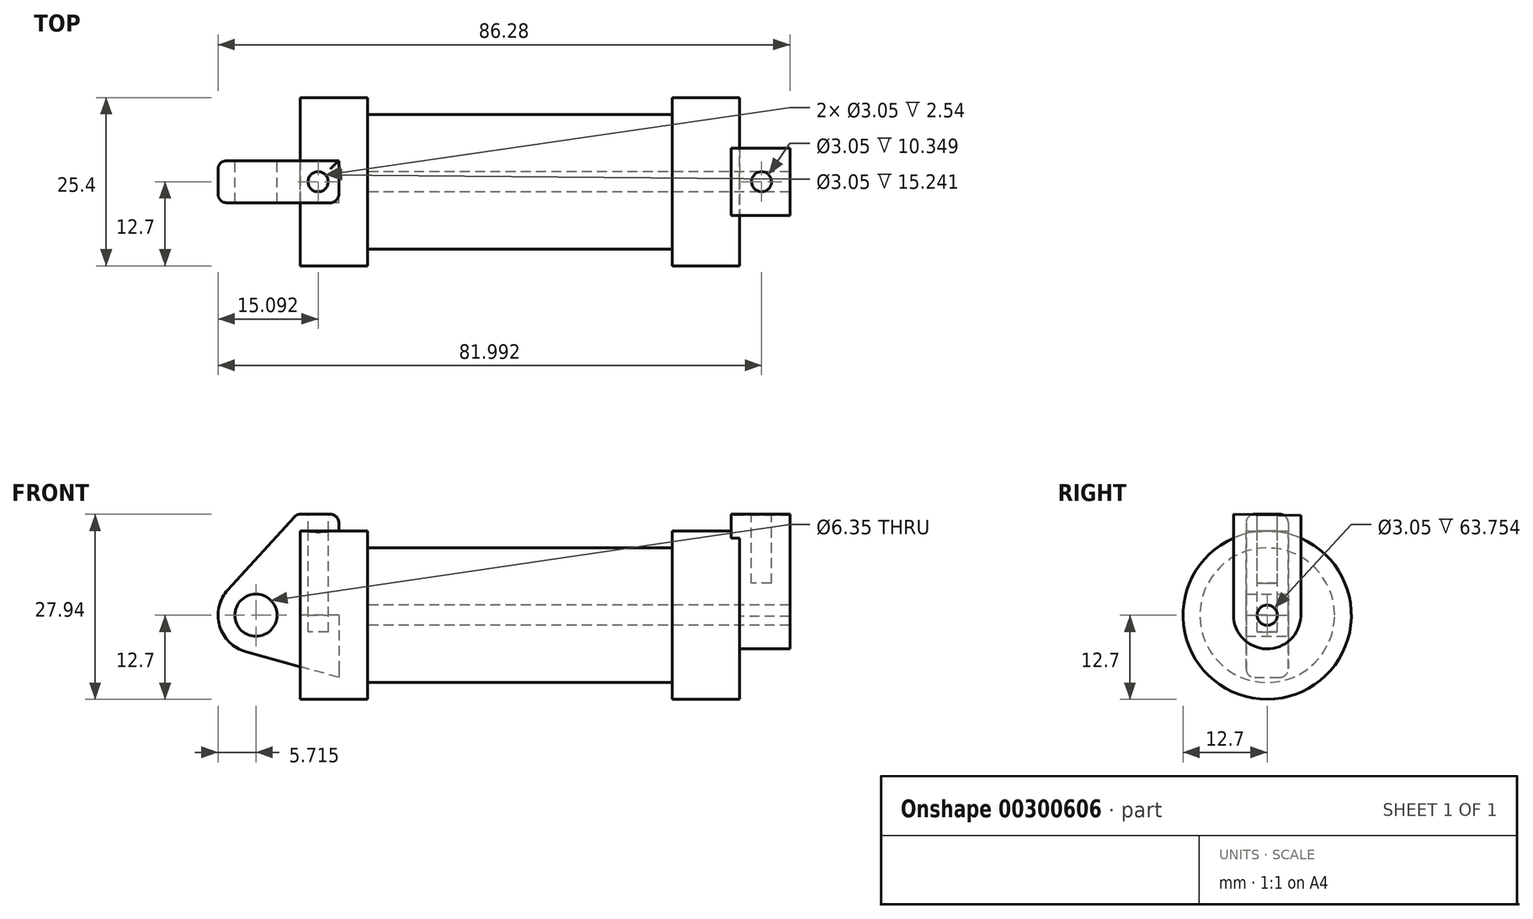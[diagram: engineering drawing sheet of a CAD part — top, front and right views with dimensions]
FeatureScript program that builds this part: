
annotation { "Feature Type Name" : "Feature", "Feature Type Description" : "" }
export const myFeature = defineFeature(function(context is Context, id is Id, definition is map)
    precondition{}
    {
        {
            var Q0;
            Q0=qCreatedBy(makeId("Front.planeOp"),FACE);
            var sketch = newSketch(context, id + "F0", { "sketchPlane" : qUnion([Q0])});
            skLineSegment(sketch, "E0", {"start": v(0, 0) * mm, "end": v(0, 12.7) * mm});
            skLineSegment(sketch, "E1", {"start": v(0, 12.7) * mm, "end": v(10.16, 12.7) * mm});
            skLineSegment(sketch, "E2", {"start": v(10.16, 12.7) * mm, "end": v(10.16, 10.16) * mm});
            skLineSegment(sketch, "E3", {"start": v(10.16, 10.16) * mm, "end": v(56.13, 10.16) * mm});
            skLineSegment(sketch, "E4", {"start": v(56.13, 10.16) * mm, "end": v(56.13, 12.7) * mm});
            skLineSegment(sketch, "E5", {"start": v(56.13, 12.7) * mm, "end": v(66.3, 12.7) * mm});
            skLineSegment(sketch, "E6", {"start": v(66.3, 12.7) * mm, "end": v(66.3, 0) * mm});
            skLineSegment(sketch, "E7", {"start": v(66.3, 0) * mm, "end": v(0, 0) * mm});
            skLineSegment(sketch, "E8", {"start": v(5.84, 15.24) * mm, "end": v(-0.5, 15.24) * mm});
            skLineSegment(sketch, "E9", {"start": v(-0.5, 15.24) * mm, "end": v(-10.88, 3.85) * mm});
            skLineSegment(sketch, "E10", {"start": v(0, 0) * mm, "end": v(-6.65, 0) * mm});
            skCircle(sketch, "E11", {"center": v(-6.65, 0) * mm, "radius": 5.72 * mm});
            skCircle(sketch, "E12", {"center": v(-6.65, 0) * mm, "radius": 3.18 * mm});
            skLineSegment(sketch, "E13", {"start": v(5.84, 15.24) * mm, "end": v(5.84, -9.4) * mm});
            skLineSegment(sketch, "E14", {"start": v(5.84, -9.4) * mm, "end": v(-8.18, -5.5) * mm});
            skSolve(sketch);
        }
        {
            var Q0;
            {var subQ0=sQuery(id+"F0.wireOp",EDGE,"E2");Q0=makeQuery(id+"F0.imprint","IMPRINT",FACE,{"disambiguationData":[TD([[makeQuery(id+"F0.imprint","IMPRINT",EDGE,{"derivedFrom":subQ0}),-1.0]])]});}
            var Q1;
            {var subQ0=sQuery(id+"F0.wireOp",EDGE,"E0");Q1=makeQuery(id+"F0.imprint","IMPRINT",FACE,{"disambiguationData":[TD([[makeQuery(id+"F0.imprint","IMPRINT",EDGE,{"derivedFrom":subQ0}),-1.0]])]});}
            var Q2;
            Q2=sQuery(id+"F0.wireOp",EDGE,"E10");
            revolve(context, id + "F1", {"entities" : qUnion([Q0, Q1]), "axis" : qUnion([Q2]), "revolveType" : RevolveType.FULL});
        }
        {
            var Q0;
            {var subQ1=sQuery(id+"F0.wireOp",EDGE,"E0");Q0=makeQuery(id+"F0.imprint","IMPRINT",FACE,{"disambiguationData":[TD([[makeQuery(id+"F0.imprint","IMPRINT",EDGE,{"derivedFrom":subQ1}),1.0]])]});}
            var Q1;
            {var subQ5=sQuery(id+"F0.wireOp",EDGE,"E12");Q1=makeQuery(id+"F0.imprint","IMPRINT",FACE,{"disambiguationData":[TD([[makeQuery(id+"F0.imprint","IMPRINT",EDGE,{"derivedFrom":subQ5}),-1.0]])]});}
            var Q2;
            {var subQ0=sQuery(id+"F0.wireOp",EDGE,"E14");Q2=makeQuery(id+"F0.imprint","IMPRINT",FACE,{"disambiguationData":[TD([[makeQuery(id+"F0.imprint","IMPRINT",EDGE,{"derivedFrom":subQ0}),-1.0]])]});}
            extrude(context, id + "F2", {"entities" : qUnion([Q0, Q1, Q2]), "endBound" : BoundingType.SYMMETRIC, "depth" : 6.35 * mm});
        }
        {
            var Q0;
            Q0=makeQuery(id+"F1.opRevolve","SWEPT_FACE",FACE,{"disambiguationData":[OSD([sQuery(id+"F0.wireOp",EDGE,"E6")])]});
            var sketch = newSketch(context, id + "F3", { "sketchPlane" : qUnion([Q0])});
            skLineSegment(sketch, "E15", {"start": v(0, 0) * mm, "end": v(0, 15.74) * mm, "construction": true});
            skCircle(sketch, "E16", {"center": v(0, 0) * mm, "radius": 1.52 * mm});
            skCircle(sketch, "E17", {"center": v(0, 0) * mm, "radius": 5.08 * mm});
            skLineSegment(sketch, "E18", {"start": v(0, 0) * mm, "end": v(-14.5, 0) * mm, "construction": true});
            skLineSegment(sketch, "E19", {"start": v(-5.08, 0) * mm, "end": v(-5.08, 15.24) * mm});
            skLineSegment(sketch, "E20", {"start": v(5.08, -0.19) * mm, "end": v(5.08, 15.05) * mm});
            skLineSegment(sketch, "E21", {"start": v(-5.08, 15.24) * mm, "end": v(5.08, 15.05) * mm});
            skSolve(sketch);
        }
        {
            var Q0;
            Q0=makeQuery(id+"F3.imprint","IMPRINT",FACE,{"disambiguationData":[TD([[makeQuery(id+"F3.imprint","IMPRINT",EDGE,{"derivedFrom":sQuery(id+"F3.wireOp",EDGE,"E16")}),-1.0]])]});
            var Q1;
            {var subQ0=sQuery(id+"F3.wireOp",EDGE,"E19");var subQ1=sQuery(id+"F3.wireOp",EDGE,"E17");var subQ2=makeQuery(id+"F3.imprint","INTERSECT",VERTEX,{"derivedFrom":[subQ1,subQ0]});Q1=makeQuery(id+"F3.imprint","IMPRINT",FACE,{"disambiguationData":[TD([[makeQuery(id+"F3.imprint","IMPRINT",EDGE,{"disambiguationData":[TD([[subQ2,1.0]])],"derivedFrom":subQ1}),-1.0]])]});}
            var Q2;
            {var subQ0=sQuery(id+"F3.wireOp",EDGE,"E21");Q2=makeQuery(id+"F3.imprint","IMPRINT",FACE,{"disambiguationData":[TD([[makeQuery(id+"F3.imprint","IMPRINT",EDGE,{"derivedFrom":subQ0}),-1.0]])]});}
            extrude(context, id + "F4", {"entities" : qUnion([Q0, Q1, Q2]), "operationType" : NewBodyOperationType.ADD, "depth" : 7.62 * mm, "hasSecondDirection" : true, "secondDirectionOppositeDirection" : true, "secondDirectionDepth" : 1.27 * mm});
        }
        {
            var Q0;
            Q0=makeQuery(id+"F4.boolean.opBoolean","SPLIT",FACE,{"disambiguationData":[TD([makeQuery(id+"F4.opExtrude","SWEPT_FACE",FACE,{"disambiguationData":[OSD([sQuery(id+"F3.wireOp",EDGE,"E16")])]})])],"derivedFrom":makeQuery(id+"F1.opRevolve","SWEPT_FACE",FACE,{"disambiguationData":[OSD([sQuery(id+"F0.wireOp",EDGE,"E6")])]})});
            var Q1;
            Q1=makeQuery(id+"F1.opRevolve","SWEPT_FACE",FACE,{"disambiguationData":[OSD([sQuery(id+"F0.wireOp",EDGE,"E2")])]});
            extrude(context, id + "F5", {"entities" : qUnion([Q0]), "operationType" : NewBodyOperationType.REMOVE, "endBound" : BoundingType.UP_TO_SURFACE, "oppositeDirection" : true, "endBoundEntityFace" : qUnion([Q1]), "depth" : 57.4 * mm});
        }
        {
            var Q0;
            Q0=makeQuery(id+"F2.opExtrude","SWEPT_FACE",FACE,{"disambiguationData":[OSD([sQuery(id+"F0.wireOp",EDGE,"E8")])]});
            var sketch = newSketch(context, id + "F6", { "sketchPlane" : qUnion([Q0])});
            skLineSegment(sketch, "E22", {"start": v(-0.5, 0) * mm, "end": v(75.76, 0) * mm, "construction": true});
            skCircle(sketch, "E23", {"center": v(2.72, 0) * mm, "radius": 1.52 * mm});
            skCircle(sketch, "E24", {"center": v(69.62, 0) * mm, "radius": 1.52 * mm});
            skSolve(sketch);
        }
        {
            var Q0;
            Q0=makeQuery(id+"F6.imprint","IMPRINT",FACE,{"disambiguationData":[TD([[makeQuery(id+"F6.imprint","IMPRINT",EDGE,{"derivedFrom":sQuery(id+"F6.wireOp",EDGE,"E24")}),1.0]])]});
            extrude(context, id + "F7", {"entities" : qUnion([Q0]), "operationType" : NewBodyOperationType.REMOVE, "oppositeDirection" : true, "depth" : 10.4 * mm});
        }
        {
            var Q0;
            Q0=makeQuery(id+"F6.imprint","IMPRINT",FACE,{"disambiguationData":[TD([[makeQuery(id+"F6.imprint","IMPRINT",EDGE,{"derivedFrom":sQuery(id+"F6.wireOp",EDGE,"E23")}),1.0]])]});
            extrude(context, id + "F8", {"entities" : qUnion([Q0]), "operationType" : NewBodyOperationType.REMOVE, "oppositeDirection" : true, "depth" : 17.78 * mm});
        }
        {
            var Q0;
            Q0=makeQuery(id+"F1.opRevolve","SWEPT_EDGE",EDGE,{"disambiguationData":[OSD([sQuery(id+"F0.wireOp",EDGE,"E4"),sQuery(id+"F0.wireOp",EDGE,"E5")])]});
            var Q1;
            Q1=makeQuery(id+"F4.boolean.opBoolean","SPLIT",FACE,{"disambiguationData":[TD([makeQuery(id+"F1.opRevolve","SWEPT_FACE",FACE,{"disambiguationData":[OSD([sQuery(id+"F0.wireOp",EDGE,"E5")])]})])],"derivedFrom":makeQuery(id+"F1.opRevolve","SWEPT_FACE",FACE,{"disambiguationData":[OSD([sQuery(id+"F0.wireOp",EDGE,"E6")])]})});
            var Q2;
            Q2=makeQuery(id+"F1.opRevolve","SWEPT_EDGE",EDGE,{"disambiguationData":[OSD([sQuery(id+"F0.wireOp",EDGE,"E1"),sQuery(id+"F0.wireOp",EDGE,"E2")])]});
            var Q3;
            Q3=makeQuery(id+"F1.opRevolve","SWEPT_EDGE",EDGE,{"disambiguationData":[OSD([sQuery(id+"F0.wireOp",EDGE,"E0"),sQuery(id+"F0.wireOp",EDGE,"E1")])]});
            var Q4;
            Q4=makeQuery(id+"F2.opExtrude","CAP_EDGE",EDGE,{"disambiguationData":[OSD([sQuery(id+"F0.wireOp",EDGE,"E9")])],"isStart":true});
            var Q5;
            Q5=makeQuery(id+"F4.opExtrude","CAP_EDGE",EDGE,{"disambiguationData":[OSD([sQuery(id+"F3.wireOp",EDGE,"E20")])],"isStart":false});
            var Q6;
            Q6=makeQuery(id+"F4.opExtrude","CAP_EDGE",EDGE,{"disambiguationData":[OSD([sQuery(id+"F3.wireOp",EDGE,"E21")])],"isStart":true});
            var Q7;
            Q7=makeQuery(id+"F4.opExtrude","SWEPT_EDGE",EDGE,{"disambiguationData":[OSD([sQuery(id+"F3.wireOp",EDGE,"E19"),sQuery(id+"F3.wireOp",EDGE,"E21")])]});
            var Q8;
            Q8=makeQuery(id+"F4.opExtrude","CAP_EDGE",EDGE,{"disambiguationData":[OSD([sQuery(id+"F3.wireOp",EDGE,"E21")])],"isStart":false});
            var Q9;
            Q9=makeQuery(id+"F4.opExtrude","SWEPT_EDGE",EDGE,{"disambiguationData":[OSD([sQuery(id+"F3.wireOp",EDGE,"E20"),sQuery(id+"F3.wireOp",EDGE,"E21")])]});
            var Q10;
            Q10=makeQuery(id+"F4.opExtrude","CAP_EDGE",EDGE,{"disambiguationData":[OSD([sQuery(id+"F3.wireOp",EDGE,"E17")])],"isStart":false});
            var Q11;
            Q11=makeQuery(id+"F4.opExtrude","CAP_EDGE",EDGE,{"disambiguationData":[OSD([sQuery(id+"F3.wireOp",EDGE,"E19")])],"isStart":false});
            var Q12;
            Q12=makeQuery(id+"F2.opExtrude","CAP_EDGE",EDGE,{"disambiguationData":[OSD([sQuery(id+"F0.wireOp",EDGE,"E11")])],"isStart":false});
            var Q13;
            Q13=makeQuery(id+"F2.opExtrude","CAP_EDGE",EDGE,{"disambiguationData":[OSD([sQuery(id+"F0.wireOp",EDGE,"E11")])],"isStart":true});
            var Q14;
            Q14=makeQuery(id+"F2.opExtrude","CAP_EDGE",EDGE,{"disambiguationData":[OSD([sQuery(id+"F0.wireOp",EDGE,"E14")])],"isStart":true});
            var Q15;
            Q15=makeQuery(id+"F2.opExtrude","CAP_EDGE",EDGE,{"disambiguationData":[OSD([sQuery(id+"F0.wireOp",EDGE,"E14")])],"isStart":false});
            var Q16;
            Q16=makeQuery(id+"F2.opExtrude","SWEPT_EDGE",EDGE,{"disambiguationData":[OSD([sQuery(id+"F0.wireOp",EDGE,"E8"),sQuery(id+"F0.wireOp",EDGE,"E9")])]});
            var Q17;
            Q17=makeQuery(id+"F2.opExtrude","CAP_EDGE",EDGE,{"disambiguationData":[OSD([sQuery(id+"F0.wireOp",EDGE,"E8")])],"isStart":false});
            var Q18;
            Q18=makeQuery(id+"F2.opExtrude","SWEPT_EDGE",EDGE,{"disambiguationData":[OSD([sQuery(id+"F0.wireOp",EDGE,"E8"),sQuery(id+"F0.wireOp",EDGE,"E13")])]});
            var Q19;
            Q19=makeQuery(id+"F2.opExtrude","CAP_EDGE",EDGE,{"disambiguationData":[OSD([sQuery(id+"F0.wireOp",EDGE,"E8")])],"isStart":true});
            var Q20;
            {var subQ0=sQuery(id+"F0.wireOp",EDGE,"E13");Q20=makeQuery(id+"F2.opExtrude","CAP_EDGE",EDGE,{"disambiguationData":[OSD([subQ0]),TDD([makeQuery(id+"F0.imprint","IMPRINT",EDGE,{"disambiguationData":[TD([[makeQuery(id+"F0.imprint","INTERSECT",VERTEX,{"derivedFrom":[sQuery(id+"F0.wireOp",EDGE,"E8"),subQ0]}),-1.0]])],"derivedFrom":subQ0})])],"isStart":false});}
            fillet(context, id + "F9", {"entities" : qUnion([Q0, Q1, Q2, Q3, Q4, Q5, Q6, Q7, Q8, Q9, Q10, Q11, Q12, Q13, Q14, Q15, Q16, Q17, Q18, Q19, Q20]), "radius" : 1.27 * mm, "tangentPropagation" : true, "allowEdgeOverflow" : false});
        }
    });
